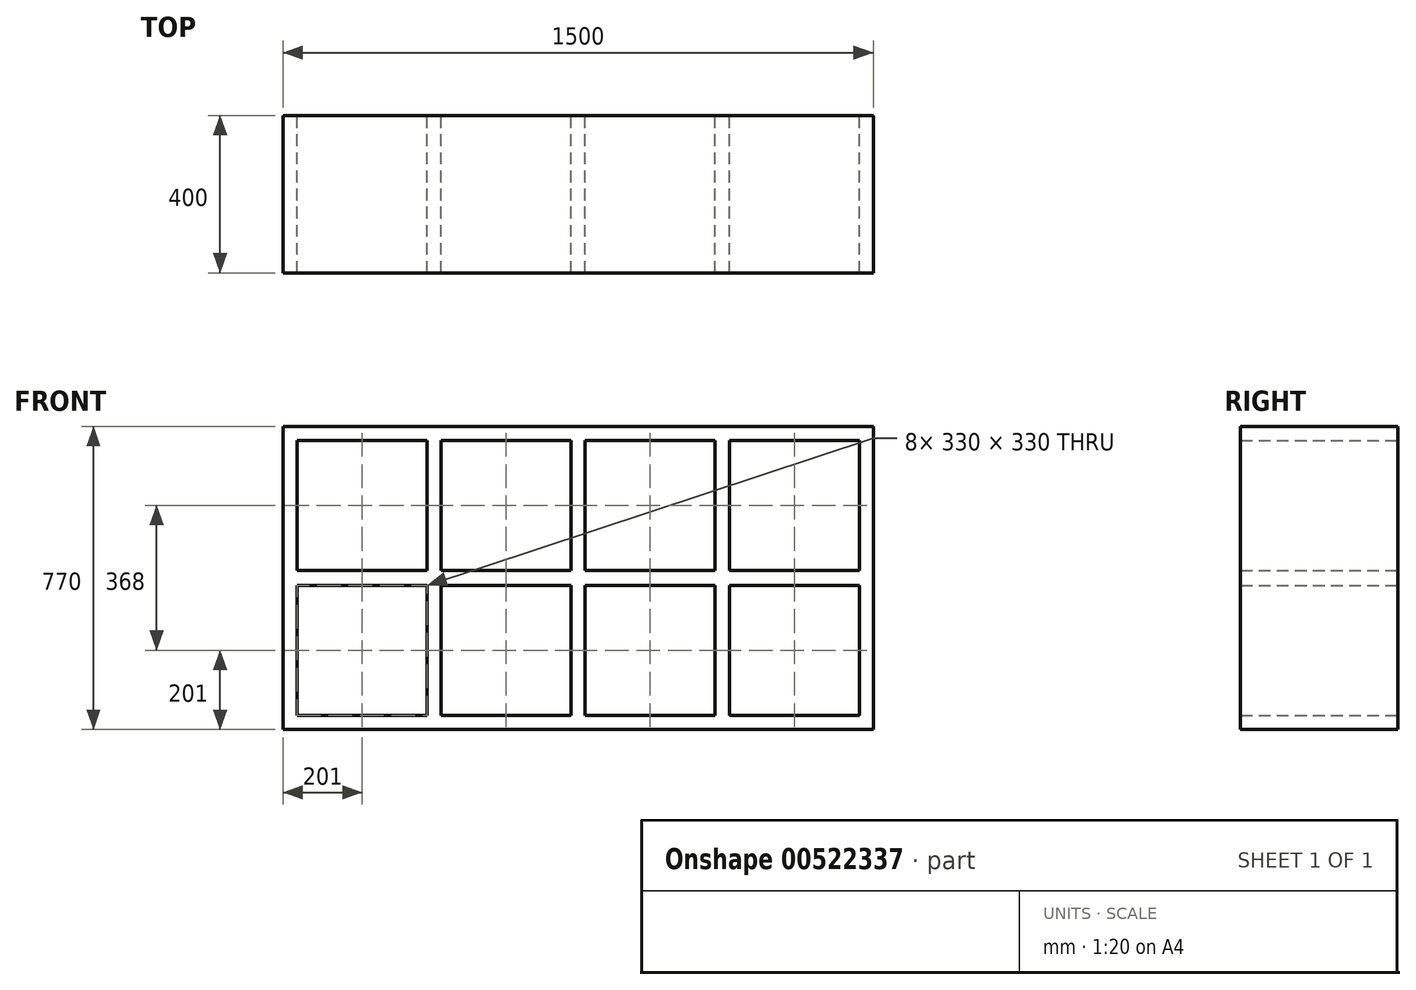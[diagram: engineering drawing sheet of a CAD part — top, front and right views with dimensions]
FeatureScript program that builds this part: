
annotation { "Feature Type Name" : "Feature", "Feature Type Description" : "" }
export const myFeature = defineFeature(function(context is Context, id is Id, definition is map)
    precondition{}
    {
        {
            var Q0;
            Q0=qCreatedBy(makeId("Front.planeOp"),FACE);
            var sketch = newSketch(context, id + "F0", { "sketchPlane" : qUnion([Q0])});
            skLineSegment(sketch, "E0.bottom", {"start": v(0, 0) * mm, "end": v(1500, 0) * mm});
            skLineSegment(sketch, "E0.top", {"start": v(0, -770) * mm, "end": v(1500, -770) * mm});
            skLineSegment(sketch, "E0.left", {"start": v(0, 0) * mm, "end": v(0, -770) * mm});
            skLineSegment(sketch, "E0.right", {"start": v(1500, 0) * mm, "end": v(1500, -770) * mm});
            skLineSegment(sketch, "E1.left", {"start": v(370, -104.63) * mm, "end": v(370, -108.63) * mm});
            skLineSegment(sketch, "E1.right", {"start": v(355.02, -104.63) * mm, "end": v(355.02, -108.63) * mm});
            skLineSegment(sketch, "E2.left", {"start": v(730, -104.63) * mm, "end": v(730, -108.63) * mm});
            skLineSegment(sketch, "E2.right", {"start": v(715.02, -104.63) * mm, "end": v(715.02, -108.63) * mm});
            skLineSegment(sketch, "E3.top", {"start": v(1079.12, -380) * mm, "end": v(1079.12, -380) * mm});
            skLineSegment(sketch, "E4.left", {"start": v(1099.12, -104.63) * mm, "end": v(1099.12, -108.63) * mm});
            skLineSegment(sketch, "E4.right", {"start": v(1084.14, -104.63) * mm, "end": v(1084.14, -108.63) * mm});
            skPoint(sketch, "E5", {"position": v(1079.12, -380) * mm});
            skLineSegment(sketch, "E6.bottom", {"start": v(1134, -36) * mm, "end": v(1464, -36) * mm});
            skLineSegment(sketch, "E6.top", {"start": v(1134, -366) * mm, "end": v(1464, -366) * mm});
            skLineSegment(sketch, "E6.left", {"start": v(1134, -36) * mm, "end": v(1134, -366) * mm});
            skLineSegment(sketch, "E6.right", {"start": v(1464, -36) * mm, "end": v(1464, -366) * mm});
            skLineSegment(sketch, "E7.left", {"start": v(1467.15, -111.62) * mm, "end": v(1467.15, -115.62) * mm});
            skLineSegment(sketch, "E7.right", {"start": v(1452.17, -111.62) * mm, "end": v(1452.17, -115.62) * mm});
            skLineSegment(sketch, "E8.left", {"start": v(408.02, -442) * mm, "end": v(408.02, -446) * mm});
            skLineSegment(sketch, "E8.right", {"start": v(393.04, -442) * mm, "end": v(393.04, -446) * mm});
            skLineSegment(sketch, "E9.bottom", {"start": v(36, -404) * mm, "end": v(366, -404) * mm});
            skLineSegment(sketch, "E9.top", {"start": v(36, -734) * mm, "end": v(366, -734) * mm});
            skLineSegment(sketch, "E9.left", {"start": v(36, -404) * mm, "end": v(36, -734) * mm});
            skLineSegment(sketch, "E9.right", {"start": v(366, -404) * mm, "end": v(366, -734) * mm});
            skLineSegment(sketch, "E10.left", {"start": v(376, -464) * mm, "end": v(376, -468) * mm});
            skLineSegment(sketch, "E10.right", {"start": v(361.02, -464) * mm, "end": v(361.02, -468) * mm});
            skLineSegment(sketch, "E11.bottom", {"start": v(402, -404) * mm, "end": v(732, -404) * mm});
            skLineSegment(sketch, "E11.top", {"start": v(402, -734) * mm, "end": v(732, -734) * mm});
            skLineSegment(sketch, "E11.left", {"start": v(402, -404) * mm, "end": v(402, -734) * mm});
            skLineSegment(sketch, "E11.right", {"start": v(732, -404) * mm, "end": v(732, -734) * mm});
            skLineSegment(sketch, "E12.left", {"start": v(734, -464) * mm, "end": v(734, -468) * mm});
            skLineSegment(sketch, "E12.right", {"start": v(719.02, -464) * mm, "end": v(719.02, -468) * mm});
            skLineSegment(sketch, "E13.bottom", {"start": v(768, -404) * mm, "end": v(1098, -404) * mm});
            skLineSegment(sketch, "E13.top", {"start": v(768, -734) * mm, "end": v(1098, -734) * mm});
            skLineSegment(sketch, "E13.left", {"start": v(768, -404) * mm, "end": v(768, -734) * mm});
            skLineSegment(sketch, "E13.right", {"start": v(1098, -404) * mm, "end": v(1098, -734) * mm});
            skLineSegment(sketch, "E14.left", {"start": v(1104, -464) * mm, "end": v(1104, -468) * mm});
            skLineSegment(sketch, "E14.right", {"start": v(1089.02, -464) * mm, "end": v(1089.02, -468) * mm});
            skLineSegment(sketch, "E15.bottom", {"start": v(1134, -404) * mm, "end": v(1464, -404) * mm});
            skLineSegment(sketch, "E15.top", {"start": v(1134, -734) * mm, "end": v(1464, -734) * mm});
            skLineSegment(sketch, "E15.left", {"start": v(1134, -404) * mm, "end": v(1134, -734) * mm});
            skLineSegment(sketch, "E15.right", {"start": v(1464, -404) * mm, "end": v(1464, -734) * mm});
            skLineSegment(sketch, "E16.left", {"start": v(1464, -464) * mm, "end": v(1464, -468) * mm});
            skLineSegment(sketch, "E16.right", {"start": v(1449.02, -464) * mm, "end": v(1449.02, -468) * mm});
            skLineSegment(sketch, "E17.bottom", {"start": v(768, -36) * mm, "end": v(1098, -36) * mm});
            skLineSegment(sketch, "E17.top", {"start": v(768, -366) * mm, "end": v(1098, -366) * mm});
            skLineSegment(sketch, "E17.left", {"start": v(768, -36) * mm, "end": v(768, -366) * mm});
            skLineSegment(sketch, "E17.right", {"start": v(1098, -36) * mm, "end": v(1098, -366) * mm});
            skLineSegment(sketch, "E18.left", {"start": v(1104, -99) * mm, "end": v(1104, -103) * mm});
            skLineSegment(sketch, "E18.right", {"start": v(1089.02, -99) * mm, "end": v(1089.02, -103) * mm});
            skLineSegment(sketch, "E19.bottom", {"start": v(402, -36) * mm, "end": v(732, -36) * mm});
            skLineSegment(sketch, "E19.top", {"start": v(402, -366) * mm, "end": v(732, -366) * mm});
            skLineSegment(sketch, "E19.left", {"start": v(402, -36) * mm, "end": v(402, -366) * mm});
            skLineSegment(sketch, "E19.right", {"start": v(732, -36) * mm, "end": v(732, -366) * mm});
            skLineSegment(sketch, "E20.left", {"start": v(734.1, -108.82) * mm, "end": v(734.1, -112.82) * mm});
            skLineSegment(sketch, "E20.right", {"start": v(719.12, -108.82) * mm, "end": v(719.12, -112.82) * mm});
            skLineSegment(sketch, "E21.bottom", {"start": v(36, -36) * mm, "end": v(366, -36) * mm});
            skLineSegment(sketch, "E21.top", {"start": v(36, -366) * mm, "end": v(366, -366) * mm});
            skLineSegment(sketch, "E21.left", {"start": v(36, -36) * mm, "end": v(36, -366) * mm});
            skLineSegment(sketch, "E21.right", {"start": v(366, -36) * mm, "end": v(366, -366) * mm});
            skLineSegment(sketch, "E22.left", {"start": v(378.08, -110.4) * mm, "end": v(378.08, -114.4) * mm});
            skLineSegment(sketch, "E22.right", {"start": v(363.1, -110.4) * mm, "end": v(363.1, -114.4) * mm});
            skSolve(sketch);
        }
        {
            var Q0;
            Q0=makeQuery(id+"F0.imprint","IMPRINT",FACE,{"disambiguationData":[TD([[makeQuery(id+"F0.imprint","IMPRINT",EDGE,{"derivedFrom":sQuery(id+"F0.wireOp",EDGE,"E0.bottom")}),-1.0]])]});
            extrude(context, id + "F1", {"entities" : qUnion([Q0]), "depth" : 400 * mm, "offsetDistance" : 25 * mm});
        }
    });
